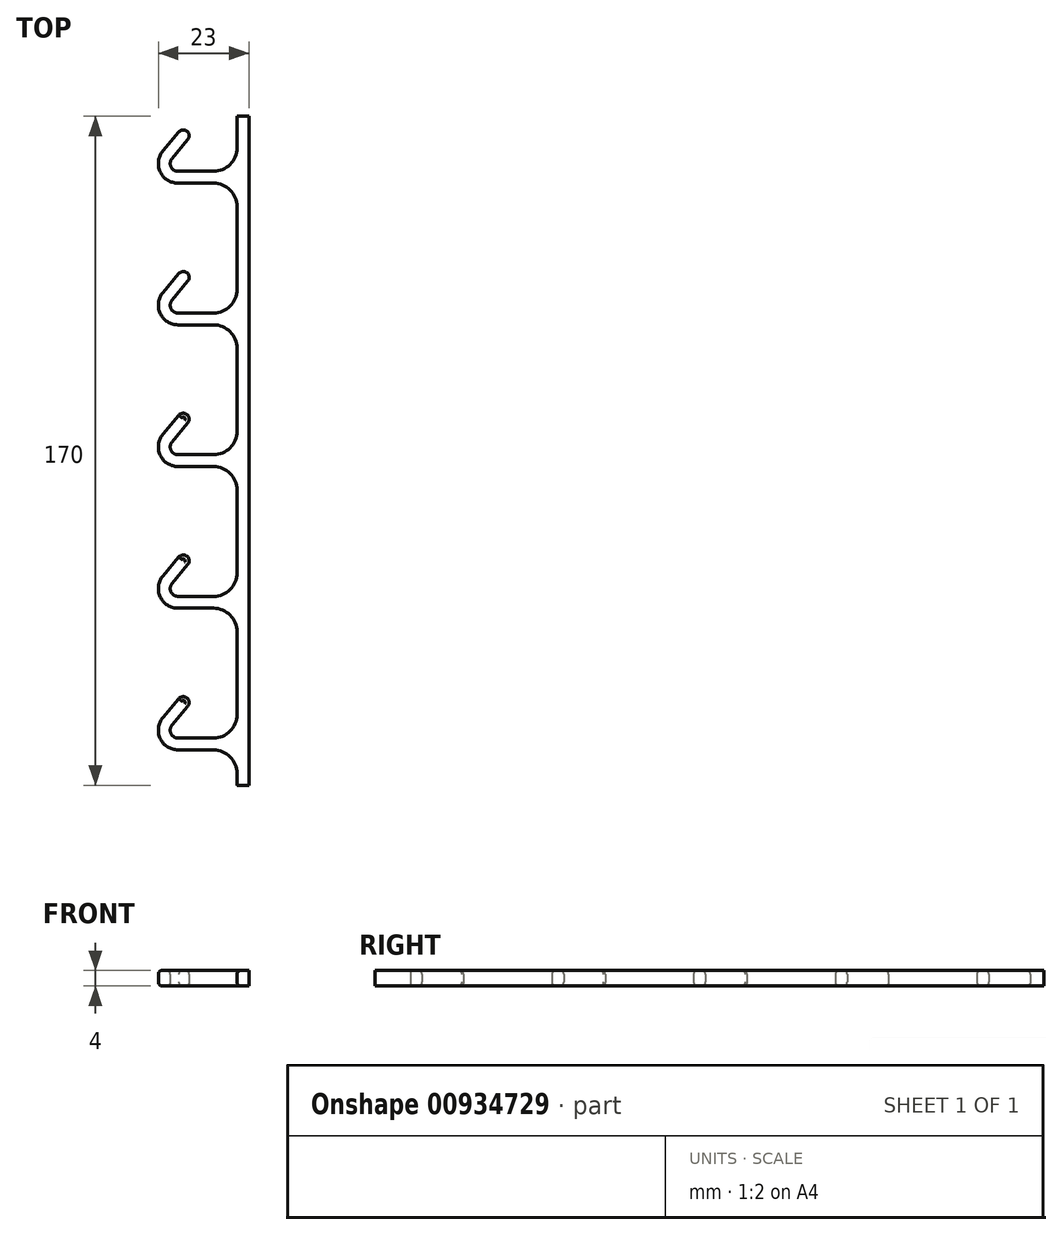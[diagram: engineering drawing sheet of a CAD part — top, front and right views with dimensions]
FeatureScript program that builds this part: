
annotation { "Feature Type Name" : "Feature", "Feature Type Description" : "" }
export const myFeature = defineFeature(function(context is Context, id is Id, definition is map)
    precondition{}
    {
        {
            var Q0;
            Q0=qCreatedBy(makeId("Top.planeOp"),FACE);
            var sketch = newSketch(context, id + "F0", { "sketchPlane" : qUnion([Q0])});
            skLineSegment(sketch, "E0.bottom", {"start": v(1.5, -85) * mm, "end": v(-1.5, -85) * mm});
            skLineSegment(sketch, "E0.top", {"start": v(1.5, 85) * mm, "end": v(-1.5, 85) * mm});
            skLineSegment(sketch, "E0.left", {"start": v(1.5, -85) * mm, "end": v(1.5, 85) * mm});
            skLineSegment(sketch, "E0.right", {"start": v(-1.5, -85) * mm, "end": v(-1.5, 85) * mm});
            skPoint(sketch, "E0.middle", {"position": v(0, 0) * mm});
            skLineSegment(sketch, "E1", {"start": v(-1.5, -76) * mm, "end": v(-16.5, -76) * mm});
            skLineSegment(sketch, "E2", {"start": v(-20.33, -67.79) * mm, "end": v(-16.31, -63) * mm});
            skPoint(sketch, "E3.visualSharp", {"position": v(-27.22, -76) * mm});
            skArc(sketch, "E3.filletArc", {"start": v(-20.33, -67.79) * mm, "mid": v(-21.03, -73.11) * mm, "end": v(-16.5, -76) * mm});
            skLineSegment(sketch, "E4.0", {"start": v(-18.03, -69.71) * mm, "end": v(-14.02, -64.93) * mm});
            skArc(sketch, "E4.1", {"start": v(-18.03, -69.71) * mm, "mid": v(-18.31, -71.85) * mm, "end": v(-16.5, -73) * mm});
            skLineSegment(sketch, "E4.2", {"start": v(-1.5, -73) * mm, "end": v(-16.5, -73) * mm});
            skArc(sketch, "E5", {"start": v(-14.02, -64.93) * mm, "mid": v(-14.2, -62.82) * mm, "end": v(-16.31, -63) * mm});
            skLineSegment(sketch, "E6.0.1.0", {"start": v(-1.5, -40) * mm, "end": v(-16.5, -40) * mm});
            skLineSegment(sketch, "E6.0.1.1", {"start": v(-1.5, -37) * mm, "end": v(-16.5, -37) * mm});
            skArc(sketch, "E6.0.1.2", {"start": v(-18.03, -33.71) * mm, "mid": v(-18.31, -35.85) * mm, "end": v(-16.5, -37) * mm});
            skArc(sketch, "E6.0.1.3", {"start": v(-20.33, -31.79) * mm, "mid": v(-21.03, -37.11) * mm, "end": v(-16.5, -40) * mm});
            skLineSegment(sketch, "E6.0.1.4", {"start": v(-18.03, -33.71) * mm, "end": v(-14.02, -28.93) * mm});
            skLineSegment(sketch, "E6.0.1.5", {"start": v(-20.33, -31.79) * mm, "end": v(-16.31, -27) * mm});
            skArc(sketch, "E6.0.1.6", {"start": v(-14.02, -28.93) * mm, "mid": v(-14.2, -26.82) * mm, "end": v(-16.31, -27) * mm});
            skLineSegment(sketch, "E6.0.2.0", {"start": v(-1.5, -4) * mm, "end": v(-16.5, -4) * mm});
            skLineSegment(sketch, "E6.0.2.1", {"start": v(-1.5, -1) * mm, "end": v(-16.5, -1) * mm});
            skArc(sketch, "E6.0.2.2", {"start": v(-18.03, 2.29) * mm, "mid": v(-18.31, 0.15) * mm, "end": v(-16.5, -1) * mm});
            skArc(sketch, "E6.0.2.3", {"start": v(-20.33, 4.21) * mm, "mid": v(-21.03, -1.11) * mm, "end": v(-16.5, -4) * mm});
            skLineSegment(sketch, "E6.0.2.4", {"start": v(-18.03, 2.29) * mm, "end": v(-14.02, 7.07) * mm});
            skLineSegment(sketch, "E6.0.2.5", {"start": v(-20.33, 4.21) * mm, "end": v(-16.31, 9) * mm});
            skArc(sketch, "E6.0.2.6", {"start": v(-14.02, 7.07) * mm, "mid": v(-14.2, 9.18) * mm, "end": v(-16.31, 9) * mm});
            skLineSegment(sketch, "E6.0.3.0", {"start": v(-1.5, 32) * mm, "end": v(-16.5, 32) * mm});
            skLineSegment(sketch, "E6.0.3.1", {"start": v(-1.5, 35) * mm, "end": v(-16.5, 35) * mm});
            skArc(sketch, "E6.0.3.2", {"start": v(-18.03, 38.29) * mm, "mid": v(-18.31, 36.15) * mm, "end": v(-16.5, 35) * mm});
            skArc(sketch, "E6.0.3.3", {"start": v(-20.33, 40.21) * mm, "mid": v(-21.03, 34.89) * mm, "end": v(-16.5, 32) * mm});
            skLineSegment(sketch, "E6.0.3.4", {"start": v(-18.03, 38.29) * mm, "end": v(-14.02, 43.07) * mm});
            skLineSegment(sketch, "E6.0.3.5", {"start": v(-20.33, 40.21) * mm, "end": v(-16.31, 45) * mm});
            skArc(sketch, "E6.0.3.6", {"start": v(-14.02, 43.07) * mm, "mid": v(-14.2, 45.18) * mm, "end": v(-16.31, 45) * mm});
            skLineSegment(sketch, "E6.0.4.0", {"start": v(-1.5, 68) * mm, "end": v(-16.5, 68) * mm});
            skLineSegment(sketch, "E6.0.4.1", {"start": v(-1.5, 71) * mm, "end": v(-16.5, 71) * mm});
            skArc(sketch, "E6.0.4.2", {"start": v(-18.03, 74.29) * mm, "mid": v(-18.31, 72.15) * mm, "end": v(-16.5, 71) * mm});
            skArc(sketch, "E6.0.4.3", {"start": v(-20.33, 76.21) * mm, "mid": v(-21.03, 70.89) * mm, "end": v(-16.5, 68) * mm});
            skLineSegment(sketch, "E6.0.4.4", {"start": v(-18.03, 74.29) * mm, "end": v(-14.02, 79.07) * mm});
            skLineSegment(sketch, "E6.0.4.5", {"start": v(-20.33, 76.21) * mm, "end": v(-16.31, 81) * mm});
            skArc(sketch, "E6.0.4.6", {"start": v(-14.02, 79.07) * mm, "mid": v(-14.2, 81.18) * mm, "end": v(-16.31, 81) * mm});
            skLineSegment(sketch, "E6.direction1", {"start": v(-16.5, -76) * mm, "end": v(13.5, -76) * mm, "construction": true});
            skLineSegment(sketch, "E6.direction2", {"start": v(-16.5, -76) * mm, "end": v(-16.5, -40) * mm, "construction": true});
            skSolve(sketch);
        }
        {
            var Q0;
            {var subQ1=sQuery(id+"F0.wireOp",EDGE,"E6.0.4.0");Q0=makeQuery(id+"F0.imprint","IMPRINT",FACE,{"disambiguationData":[TD([[makeQuery(id+"F0.imprint","IMPRINT",EDGE,{"derivedFrom":subQ1}),-1.0]])]});}
            var Q1;
            {var subQ8=sQuery(id+"F0.wireOp",EDGE,"E0.bottom");Q1=makeQuery(id+"F0.imprint","IMPRINT",FACE,{"disambiguationData":[TD([[makeQuery(id+"F0.imprint","IMPRINT",EDGE,{"derivedFrom":subQ8}),-1.0]])]});}
            var Q2;
            {var subQ1=sQuery(id+"F0.wireOp",EDGE,"E6.0.3.0");Q2=makeQuery(id+"F0.imprint","IMPRINT",FACE,{"disambiguationData":[TD([[makeQuery(id+"F0.imprint","IMPRINT",EDGE,{"derivedFrom":subQ1}),-1.0]])]});}
            var Q3;
            {var subQ0=sQuery(id+"F0.wireOp",EDGE,"E6.0.2.0");Q3=makeQuery(id+"F0.imprint","IMPRINT",FACE,{"disambiguationData":[TD([[makeQuery(id+"F0.imprint","IMPRINT",EDGE,{"derivedFrom":subQ0}),-1.0]])]});}
            var Q4;
            {var subQ1=sQuery(id+"F0.wireOp",EDGE,"E6.0.1.0");Q4=makeQuery(id+"F0.imprint","IMPRINT",FACE,{"disambiguationData":[TD([[makeQuery(id+"F0.imprint","IMPRINT",EDGE,{"derivedFrom":subQ1}),-1.0]])]});}
            var Q5;
            {var subQ0=sQuery(id+"F0.wireOp",EDGE,"E1");Q5=makeQuery(id+"F0.imprint","IMPRINT",FACE,{"disambiguationData":[TD([[makeQuery(id+"F0.imprint","IMPRINT",EDGE,{"derivedFrom":subQ0}),-1.0]])]});}
            extrude(context, id + "F1", {"entities" : qUnion([Q0, Q1, Q2, Q3, Q4, Q5]), "depth" : 4 * mm, "offsetDistance" : 25 * mm});
        }
        {
            var Q0;
            Q0=makeQuery(id+"F1.opExtrude","SWEPT_EDGE",EDGE,{"disambiguationData":[OSD([sQuery(id+"F0.wireOp",EDGE,"E0.right"),sQuery(id+"F0.wireOp",EDGE,"E6.0.1.0")])]});
            var Q1;
            Q1=makeQuery(id+"F1.opExtrude","SWEPT_EDGE",EDGE,{"disambiguationData":[OSD([sQuery(id+"F0.wireOp",EDGE,"E0.right"),sQuery(id+"F0.wireOp",EDGE,"E1")])]});
            var Q2;
            Q2=makeQuery(id+"F1.opExtrude","SWEPT_EDGE",EDGE,{"disambiguationData":[OSD([sQuery(id+"F0.wireOp",EDGE,"E0.right"),sQuery(id+"F0.wireOp",EDGE,"E4.2")])]});
            var Q3;
            Q3=makeQuery(id+"F1.opExtrude","SWEPT_EDGE",EDGE,{"disambiguationData":[OSD([sQuery(id+"F0.wireOp",EDGE,"E0.right"),sQuery(id+"F0.wireOp",EDGE,"E6.0.1.1")])]});
            var Q4;
            Q4=makeQuery(id+"F1.opExtrude","SWEPT_EDGE",EDGE,{"disambiguationData":[OSD([sQuery(id+"F0.wireOp",EDGE,"E0.right"),sQuery(id+"F0.wireOp",EDGE,"E6.0.2.1")])]});
            var Q5;
            Q5=makeQuery(id+"F1.opExtrude","SWEPT_EDGE",EDGE,{"disambiguationData":[OSD([sQuery(id+"F0.wireOp",EDGE,"E0.right"),sQuery(id+"F0.wireOp",EDGE,"E6.0.2.0")])]});
            var Q6;
            Q6=makeQuery(id+"F1.opExtrude","SWEPT_EDGE",EDGE,{"disambiguationData":[OSD([sQuery(id+"F0.wireOp",EDGE,"E0.right"),sQuery(id+"F0.wireOp",EDGE,"E6.0.3.0")])]});
            var Q7;
            Q7=makeQuery(id+"F1.opExtrude","SWEPT_EDGE",EDGE,{"disambiguationData":[OSD([sQuery(id+"F0.wireOp",EDGE,"E0.right"),sQuery(id+"F0.wireOp",EDGE,"E6.0.4.0")])]});
            var Q8;
            Q8=makeQuery(id+"F1.opExtrude","SWEPT_EDGE",EDGE,{"disambiguationData":[OSD([sQuery(id+"F0.wireOp",EDGE,"E0.right"),sQuery(id+"F0.wireOp",EDGE,"E6.0.3.1")])]});
            var Q9;
            Q9=makeQuery(id+"F1.opExtrude","SWEPT_EDGE",EDGE,{"disambiguationData":[OSD([sQuery(id+"F0.wireOp",EDGE,"E0.right"),sQuery(id+"F0.wireOp",EDGE,"E6.0.4.1")])]});
            fillet(context, id + "F2", {"entities" : qUnion([Q0, Q1, Q2, Q3, Q4, Q5, Q6, Q7, Q8, Q9]), "radius" : 6 * mm, "tangentPropagation" : true, "allowEdgeOverflow" : false});
        }
        {
            var Q0;
            {var subQ0=sQuery(id+"F0.wireOp",EDGE,"E6.0.2.1");var subQ1=sQuery(id+"F0.wireOp",EDGE,"E0.right");Q0=makeQuery(id+"F2.opFillet","BLEND_EDGE",EDGE,{"blendedFrom":[makeQuery(id+"F1.opExtrude","SWEPT_EDGE",EDGE,{"disambiguationData":[OSD([subQ1,subQ0])]}),makeQuery(id+"F1.opExtrude","CAP_FACE",FACE,{"disambiguationData":[OSD([sQuery(id+"F0.wireOp",EDGE,"E0.bottom"),sQuery(id+"F0.wireOp",EDGE,"E0.top"),sQuery(id+"F0.wireOp",EDGE,"E0.left"),subQ1,sQuery(id+"F0.wireOp",EDGE,"E1"),sQuery(id+"F0.wireOp",EDGE,"E2"),sQuery(id+"F0.wireOp",EDGE,"E3.filletArc"),sQuery(id+"F0.wireOp",EDGE,"E4.0"),sQuery(id+"F0.wireOp",EDGE,"E4.1"),sQuery(id+"F0.wireOp",EDGE,"E4.2"),sQuery(id+"F0.wireOp",EDGE,"E5"),sQuery(id+"F0.wireOp",EDGE,"E6.0.1.0"),sQuery(id+"F0.wireOp",EDGE,"E6.0.1.1"),sQuery(id+"F0.wireOp",EDGE,"E6.0.1.2"),sQuery(id+"F0.wireOp",EDGE,"E6.0.1.3"),sQuery(id+"F0.wireOp",EDGE,"E6.0.1.4"),sQuery(id+"F0.wireOp",EDGE,"E6.0.1.5"),sQuery(id+"F0.wireOp",EDGE,"E6.0.1.6"),sQuery(id+"F0.wireOp",EDGE,"E6.0.2.0"),subQ0,sQuery(id+"F0.wireOp",EDGE,"E6.0.2.2"),sQuery(id+"F0.wireOp",EDGE,"E6.0.2.3"),sQuery(id+"F0.wireOp",EDGE,"E6.0.2.4"),sQuery(id+"F0.wireOp",EDGE,"E6.0.2.5"),sQuery(id+"F0.wireOp",EDGE,"E6.0.2.6"),sQuery(id+"F0.wireOp",EDGE,"E6.0.3.0"),sQuery(id+"F0.wireOp",EDGE,"E6.0.3.1"),sQuery(id+"F0.wireOp",EDGE,"E6.0.3.2"),sQuery(id+"F0.wireOp",EDGE,"E6.0.3.3"),sQuery(id+"F0.wireOp",EDGE,"E6.0.3.4"),sQuery(id+"F0.wireOp",EDGE,"E6.0.3.5"),sQuery(id+"F0.wireOp",EDGE,"E6.0.3.6"),sQuery(id+"F0.wireOp",EDGE,"E6.0.4.0"),sQuery(id+"F0.wireOp",EDGE,"E6.0.4.1"),sQuery(id+"F0.wireOp",EDGE,"E6.0.4.2"),sQuery(id+"F0.wireOp",EDGE,"E6.0.4.3"),sQuery(id+"F0.wireOp",EDGE,"E6.0.4.4"),sQuery(id+"F0.wireOp",EDGE,"E6.0.4.5"),sQuery(id+"F0.wireOp",EDGE,"E6.0.4.6")])],"isStart":true})],"blendedInto":[makeQuery(id+"F1.opExtrude","CAP_FACE",FACE,{"disambiguationData":[OSD([sQuery(id+"F0.wireOp",EDGE,"E0.bottom"),sQuery(id+"F0.wireOp",EDGE,"E0.top"),sQuery(id+"F0.wireOp",EDGE,"E0.left"),subQ1,sQuery(id+"F0.wireOp",EDGE,"E1"),sQuery(id+"F0.wireOp",EDGE,"E2"),sQuery(id+"F0.wireOp",EDGE,"E3.filletArc"),sQuery(id+"F0.wireOp",EDGE,"E4.0"),sQuery(id+"F0.wireOp",EDGE,"E4.1"),sQuery(id+"F0.wireOp",EDGE,"E4.2"),sQuery(id+"F0.wireOp",EDGE,"E5"),sQuery(id+"F0.wireOp",EDGE,"E6.0.1.0"),sQuery(id+"F0.wireOp",EDGE,"E6.0.1.1"),sQuery(id+"F0.wireOp",EDGE,"E6.0.1.2"),sQuery(id+"F0.wireOp",EDGE,"E6.0.1.3"),sQuery(id+"F0.wireOp",EDGE,"E6.0.1.4"),sQuery(id+"F0.wireOp",EDGE,"E6.0.1.5"),sQuery(id+"F0.wireOp",EDGE,"E6.0.1.6"),sQuery(id+"F0.wireOp",EDGE,"E6.0.2.0"),subQ0,sQuery(id+"F0.wireOp",EDGE,"E6.0.2.2"),sQuery(id+"F0.wireOp",EDGE,"E6.0.2.3"),sQuery(id+"F0.wireOp",EDGE,"E6.0.2.4"),sQuery(id+"F0.wireOp",EDGE,"E6.0.2.5"),sQuery(id+"F0.wireOp",EDGE,"E6.0.2.6"),sQuery(id+"F0.wireOp",EDGE,"E6.0.3.0"),sQuery(id+"F0.wireOp",EDGE,"E6.0.3.1"),sQuery(id+"F0.wireOp",EDGE,"E6.0.3.2"),sQuery(id+"F0.wireOp",EDGE,"E6.0.3.3"),sQuery(id+"F0.wireOp",EDGE,"E6.0.3.4"),sQuery(id+"F0.wireOp",EDGE,"E6.0.3.5"),sQuery(id+"F0.wireOp",EDGE,"E6.0.3.6"),sQuery(id+"F0.wireOp",EDGE,"E6.0.4.0"),sQuery(id+"F0.wireOp",EDGE,"E6.0.4.1"),sQuery(id+"F0.wireOp",EDGE,"E6.0.4.2"),sQuery(id+"F0.wireOp",EDGE,"E6.0.4.3"),sQuery(id+"F0.wireOp",EDGE,"E6.0.4.4"),sQuery(id+"F0.wireOp",EDGE,"E6.0.4.5"),sQuery(id+"F0.wireOp",EDGE,"E6.0.4.6")])],"isStart":true})]});}
            var Q1;
            {var subQ0=sQuery(id+"F0.wireOp",EDGE,"E0.right");Q1=makeQuery(id+"F1.opExtrude","CAP_EDGE",EDGE,{"disambiguationData":[OSD([subQ0]),TDD([makeQuery(id+"F0.imprint","IMPRINT",EDGE,{"disambiguationData":[TD([[makeQuery(id+"F0.imprint","INTERSECT",VERTEX,{"derivedFrom":[subQ0,sQuery(id+"F0.wireOp",EDGE,"E6.0.2.1")]}),-1.0]])],"derivedFrom":subQ0})])],"isStart":false});}
            fillet(context, id + "F3", {"entities" : qUnion([Q0, Q1]), "radius" : 1 * mm, "tangentPropagation" : true, "allowEdgeOverflow" : false});
        }
    });
